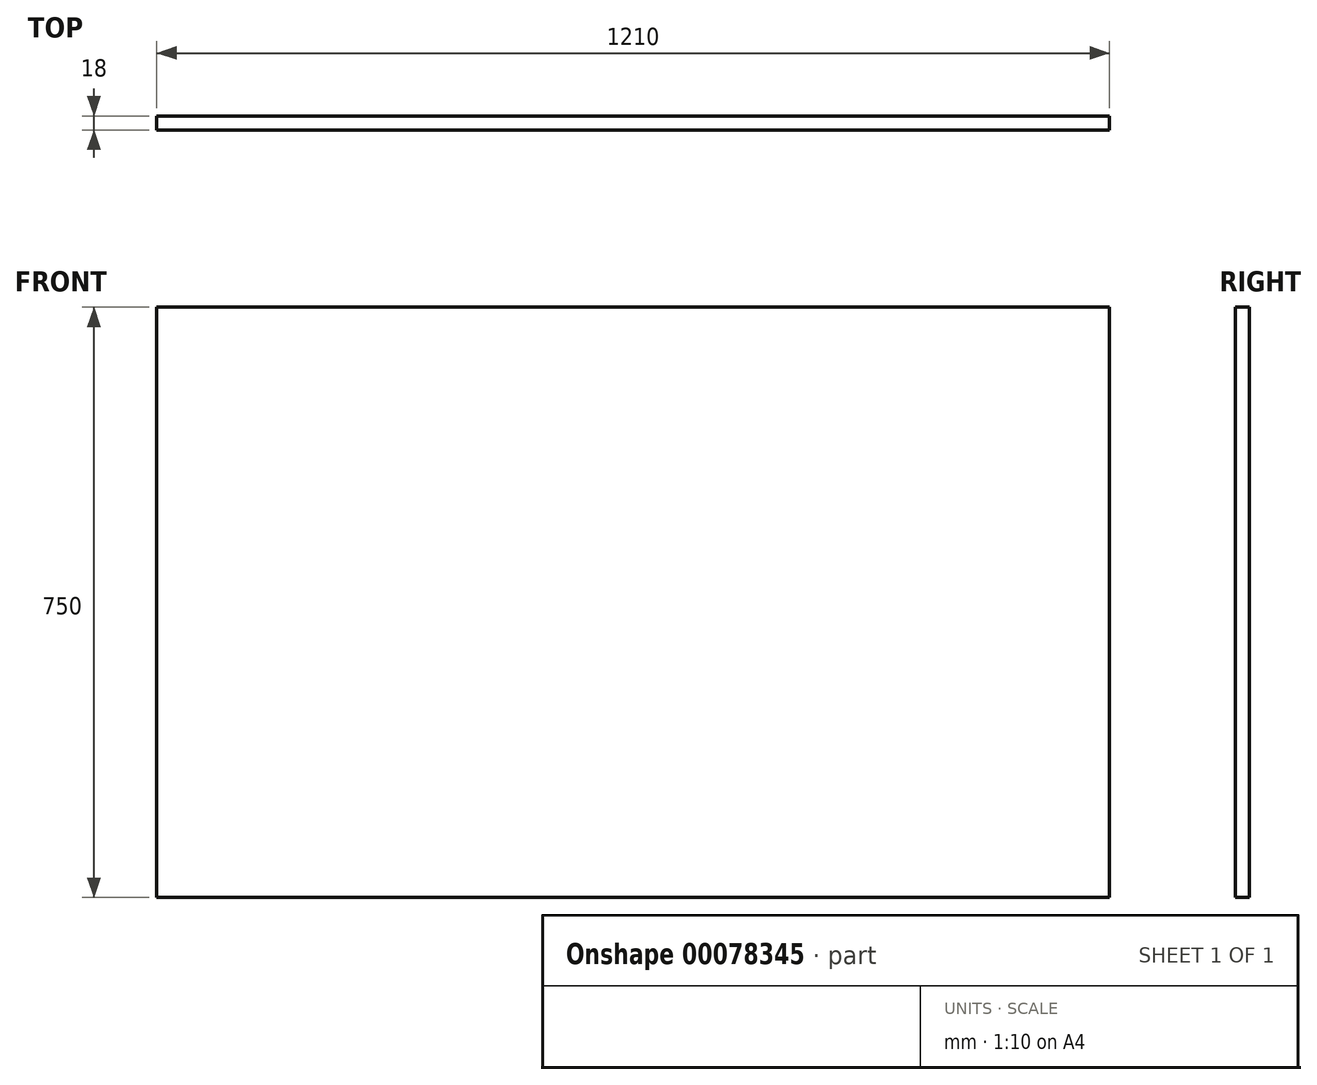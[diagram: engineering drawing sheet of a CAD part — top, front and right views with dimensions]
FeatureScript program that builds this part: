
annotation { "Feature Type Name" : "Feature", "Feature Type Description" : "" }
export const myFeature = defineFeature(function(context is Context, id is Id, definition is map)
    precondition{}
    {
        {
            var Q0;
            Q0=qCreatedBy(makeId("Front.planeOp"),FACE);
            var sketch = newSketch(context, id + "F0", { "sketchPlane" : qUnion([Q0])});
            skLineSegment(sketch, "E0.bottom", {"start": v(-605, 330.85) * mm, "end": v(605, 330.85) * mm});
            skLineSegment(sketch, "E0.top", {"start": v(-605, -419.15) * mm, "end": v(605, -419.15) * mm});
            skLineSegment(sketch, "E0.left", {"start": v(-605, 330.85) * mm, "end": v(-605, -419.15) * mm});
            skLineSegment(sketch, "E0.right", {"start": v(605, 330.85) * mm, "end": v(605, -419.15) * mm});
            skLineSegment(sketch, "E1", {"start": v(0, 0) * mm, "end": v(0, 285.72) * mm, "construction": true});
            skSolve(sketch);
        }
        {
            var Q0;
            Q0=makeQuery(id+"F0.imprint","IMPRINT",FACE,{"disambiguationData":[TD([[makeQuery(id+"F0.imprint","IMPRINT",EDGE,{"derivedFrom":sQuery(id+"F0.wireOp",EDGE,"E0.bottom")}),-1.0]])]});
            extrude(context, id + "F1", {"entities" : qUnion([Q0]), "depth" : 18 * mm});
        }
    });
